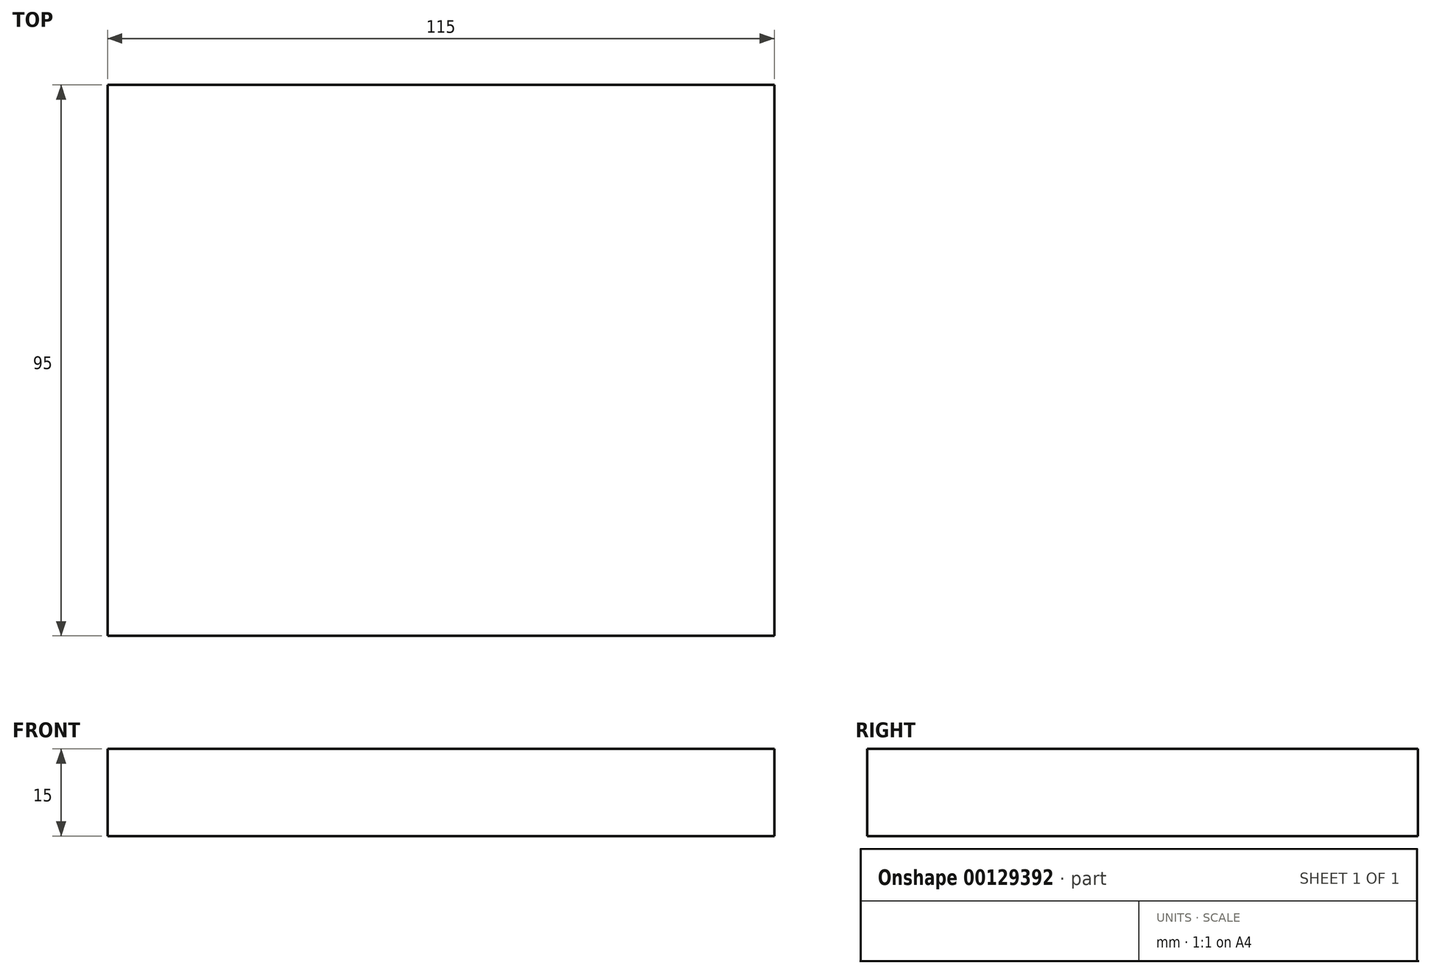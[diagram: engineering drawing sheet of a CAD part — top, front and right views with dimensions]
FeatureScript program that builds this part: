
annotation { "Feature Type Name" : "Feature", "Feature Type Description" : "" }
export const myFeature = defineFeature(function(context is Context, id is Id, definition is map)
    precondition{}
    {
        {
            var Q0;
            Q0=qCreatedBy(makeId("Top.planeOp"),FACE);
            var sketch = newSketch(context, id + "F0", { "sketchPlane" : qUnion([Q0])});
            skLineSegment(sketch, "E0.bottom", {"start": v(-57.5, -47.5) * mm, "end": v(57.5, -47.5) * mm});
            skLineSegment(sketch, "E0.top", {"start": v(-57.5, 47.5) * mm, "end": v(57.5, 47.5) * mm});
            skLineSegment(sketch, "E0.left", {"start": v(-57.5, -47.5) * mm, "end": v(-57.5, 47.5) * mm});
            skLineSegment(sketch, "E0.right", {"start": v(57.5, -47.5) * mm, "end": v(57.5, 47.5) * mm});
            skPoint(sketch, "E0.middle", {"position": v(0, 0) * mm});
            skSolve(sketch);
        }
        {
            var Q0;
            Q0=makeQuery(id+"F0.imprint","IMPRINT",FACE,{"disambiguationData":[TD([[makeQuery(id+"F0.imprint","IMPRINT",EDGE,{"derivedFrom":sQuery(id+"F0.wireOp",EDGE,"E0.bottom")}),1.0]])]});
            extrude(context, id + "F1", {"entities" : qUnion([Q0]), "depth" : 15 * mm});
        }
    });
